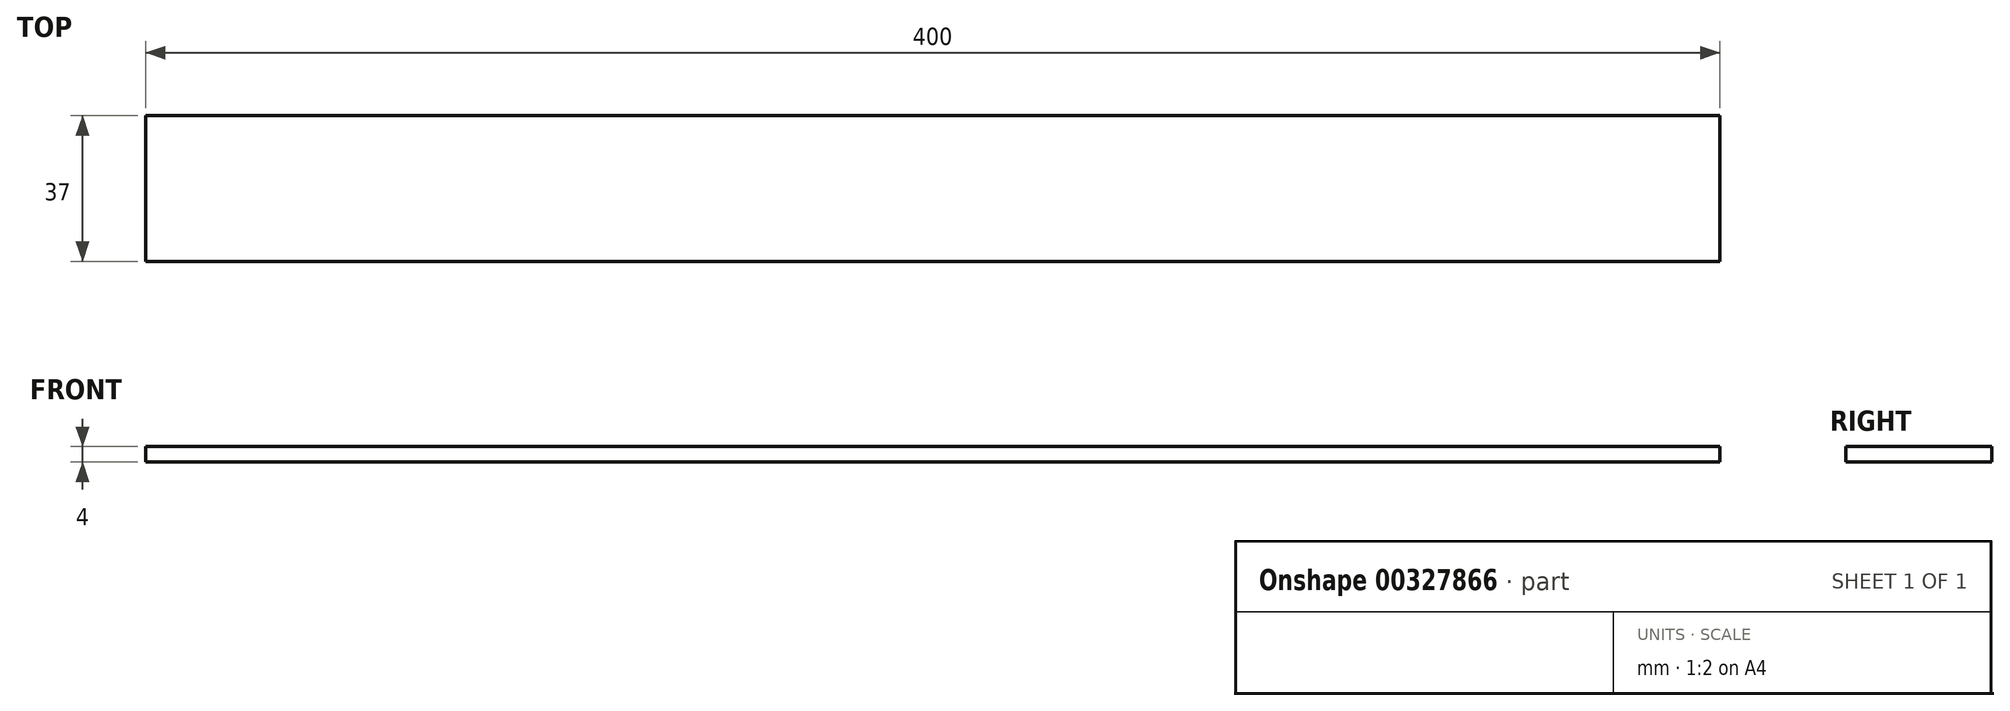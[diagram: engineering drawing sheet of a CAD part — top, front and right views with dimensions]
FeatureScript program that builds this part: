
annotation { "Feature Type Name" : "Feature", "Feature Type Description" : "" }
export const myFeature = defineFeature(function(context is Context, id is Id, definition is map)
    precondition{}
    {
        {
            var Q0;
            Q0=qCreatedBy(makeId("Top.planeOp"),FACE);
            var sketch = newSketch(context, id + "F0", { "sketchPlane" : qUnion([Q0])});
            skLineSegment(sketch, "E0.bottom", {"start": v(0, 0) * mm, "end": v(400, 0) * mm});
            skLineSegment(sketch, "E0.top", {"start": v(0, 37) * mm, "end": v(400, 37) * mm});
            skLineSegment(sketch, "E0.left", {"start": v(0, 0) * mm, "end": v(0, 37) * mm});
            skLineSegment(sketch, "E0.right", {"start": v(400, 0) * mm, "end": v(400, 37) * mm});
            skSolve(sketch);
        }
        {
            var Q0;
            Q0 = qSketchRegion(id + "F0", true);
            extrude(context, id + "F1", {"entities" : qUnion([Q0]), "depth" : 4 * mm});
        }
    });
